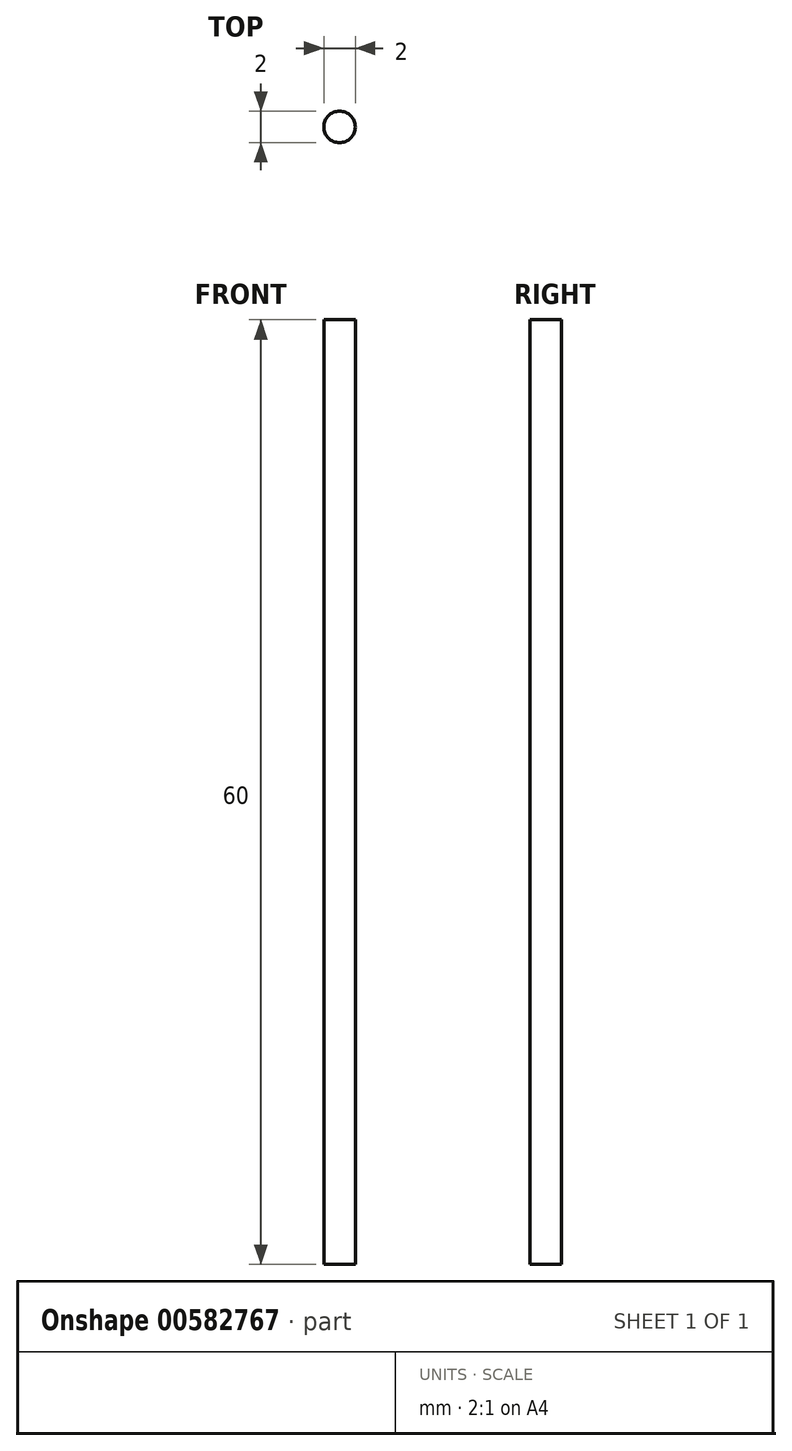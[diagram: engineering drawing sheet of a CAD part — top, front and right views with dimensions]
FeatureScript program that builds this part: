
annotation { "Feature Type Name" : "Feature", "Feature Type Description" : "" }
export const myFeature = defineFeature(function(context is Context, id is Id, definition is map)
    precondition{}
    {
        {
            var Q0;
            Q0=qCreatedBy(makeId("Top.planeOp"),FACE);
            var sketch = newSketch(context, id + "F0", { "sketchPlane" : qUnion([Q0])});
            skCircle(sketch, "E0", {"center": v(0, 0) * mm, "radius": 1 * mm});
            skSolve(sketch);
        }
        {
            var Q0;
            Q0=makeQuery(id+"F0.imprint","IMPRINT",FACE,{"disambiguationData":[TD([[makeQuery(id+"F0.imprint","IMPRINT",EDGE,{"derivedFrom":sQuery(id+"F0.wireOp",EDGE,"E0")}),1.0]])]});
            extrude(context, id + "F1", {"entities" : qUnion([Q0]), "depth" : 60 * mm});
        }
    });
